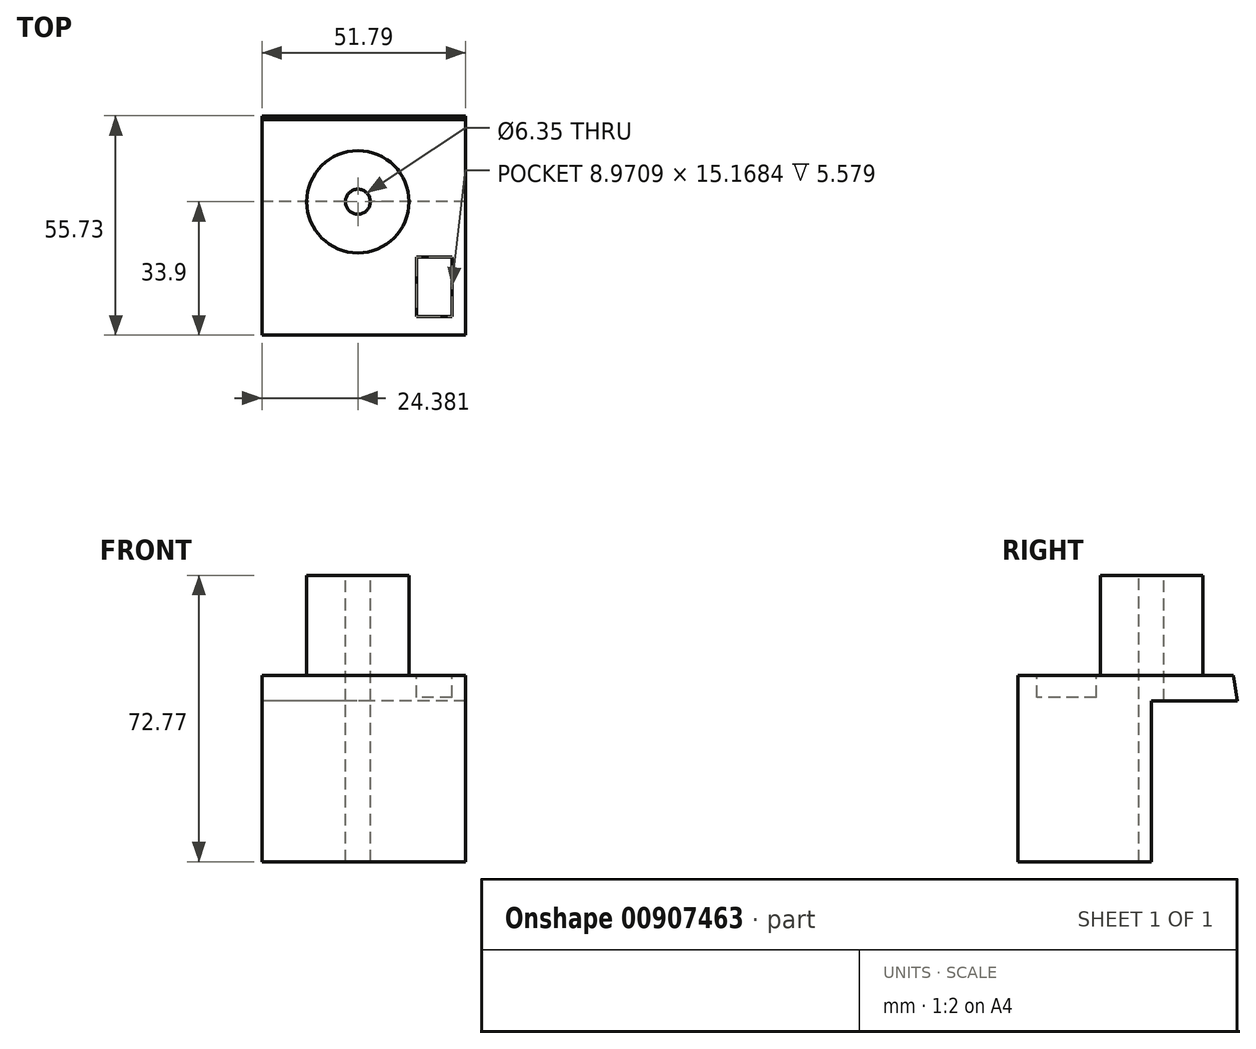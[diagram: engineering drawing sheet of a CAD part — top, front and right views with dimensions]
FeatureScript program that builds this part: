
annotation { "Feature Type Name" : "Feature", "Feature Type Description" : "" }
export const myFeature = defineFeature(function(context is Context, id is Id, definition is map)
    precondition{}
    {
        {
            var Q0;
            Q0=qCreatedBy(makeId("Right.planeOp"),FACE);
            var sketch = newSketch(context, id + "F0", { "sketchPlane" : qUnion([Q0])});
            skLineSegment(sketch, "E0", {"start": v(20.85, 6.5) * mm, "end": v(-33.9, 6.5) * mm});
            skLineSegment(sketch, "E1", {"start": v(-33.9, 6.5) * mm, "end": v(-33.9, -40.87) * mm});
            skLineSegment(sketch, "E2", {"start": v(-33.9, -40.87) * mm, "end": v(0, -40.87) * mm});
            skLineSegment(sketch, "E3", {"start": v(0, -40.87) * mm, "end": v(0, 0) * mm});
            skLineSegment(sketch, "E4", {"start": v(0, 0) * mm, "end": v(21.83, 0) * mm});
            skLineSegment(sketch, "E5", {"start": v(21.83, 0) * mm, "end": v(20.85, 6.5) * mm});
            skSolve(sketch);
        }
        {
            var Q0;
            Q0=makeQuery(id+"F0.imprint","IMPRINT",FACE,{"disambiguationData":[TD([[makeQuery(id+"F0.imprint","IMPRINT",EDGE,{"derivedFrom":sQuery(id+"F0.wireOp",EDGE,"E0")}),1.0]])]});
            extrude(context, id + "F1", {"entities" : qUnion([Q0]), "depth" : 51.8 * mm, "offsetDistance" : 25.4 * mm});
        }
        {
            var Q0;
            Q0=makeQuery(id+"F1.opExtrude","SWEPT_FACE",FACE,{"disambiguationData":[OSD([sQuery(id+"F0.wireOp",EDGE,"E0")])]});
            var sketch = newSketch(context, id + "F2", { "sketchPlane" : qUnion([Q0])});
            skCircle(sketch, "E6", {"center": v(24.38, 0) * mm, "radius": 13 * mm});
            skSolve(sketch);
        }
        {
            var Q0;
            Q0 = qSketchRegion(id + "F2", true);
            extrude(context, id + "F3", {"entities" : qUnion([Q0]), "operationType" : NewBodyOperationType.ADD, "depth" : 25.4 * mm, "offsetDistance" : 25.4 * mm});
        }
        {
            var Q0;
            Q0=makeQuery(id+"F3.opExtrude","CAP_FACE",FACE,{"disambiguationData":[OSD([sQuery(id+"F2.wireOp",EDGE,"E6")])],"isStart":false});
            var sketch = newSketch(context, id + "F4", { "sketchPlane" : qUnion([Q0])});
            skCircle(sketch, "E7", {"center": v(24.38, 0) * mm, "radius": 5.53 * mm});
            skSolve(sketch);
        }
        {
            var Q0;
            Q0=sQuery(id+"F4.wireOp",VERTEX,"E7.center");
            var Q1;
            Q1=makeQuery(id+"F1.opExtrude","SWEPT_BODY",BODY,{"disambiguationData":[OSD([sQuery(id+"F0.wireOp",EDGE,"E0"),sQuery(id+"F0.wireOp",EDGE,"E1"),sQuery(id+"F0.wireOp",EDGE,"E2"),sQuery(id+"F0.wireOp",EDGE,"E3"),sQuery(id+"F0.wireOp",EDGE,"E4"),sQuery(id+"F0.wireOp",EDGE,"E5")])]});
            hole(context, id + "F5", {"style" : HoleStyle.SIMPLE, "endStyle" : HoleEndStyle.THROUGH, "holeDiameter" : 6.35 * mm, "majorDiameter" : 6.35 * mm, "isTappedThrough" : true, "tappedDepth" : 12.7 * mm, "tapClearance" : 3, "locations" : qUnion([Q0]), "scope" : qUnion([Q1])});
        }
        {
            var Q0;
            Q0=makeQuery(id+"F1.opExtrude","SWEPT_FACE",FACE,{"disambiguationData":[OSD([sQuery(id+"F0.wireOp",EDGE,"E0")])]});
            var sketch = newSketch(context, id + "F6", { "sketchPlane" : qUnion([Q0])});
            skLineSegment(sketch, "E8.bottom", {"start": v(48.26, -14) * mm, "end": v(39.29, -14) * mm});
            skLineSegment(sketch, "E8.top", {"start": v(48.26, -29.17) * mm, "end": v(39.29, -29.17) * mm});
            skLineSegment(sketch, "E8.left", {"start": v(48.26, -14) * mm, "end": v(48.26, -29.17) * mm});
            skLineSegment(sketch, "E8.right", {"start": v(39.29, -14) * mm, "end": v(39.29, -29.17) * mm});
            skSolve(sketch);
        }
        {
            var Q0;
            Q0 = qSketchRegion(id + "F6", true);
            extrude(context, id + "F7", {"entities" : qUnion([Q0]), "operationType" : NewBodyOperationType.REMOVE, "oppositeDirection" : true, "depth" : 5.58 * mm, "offsetDistance" : 25.4 * mm});
        }
    });
